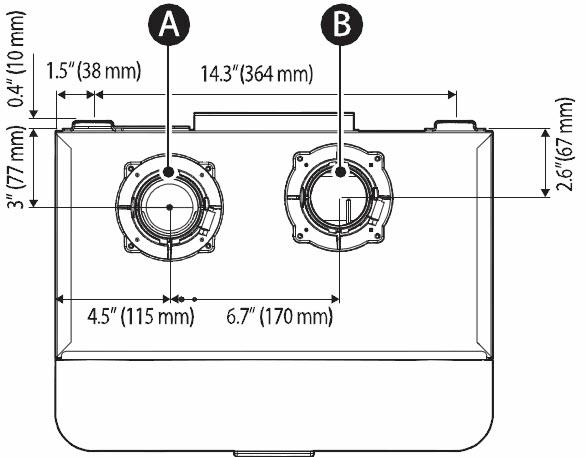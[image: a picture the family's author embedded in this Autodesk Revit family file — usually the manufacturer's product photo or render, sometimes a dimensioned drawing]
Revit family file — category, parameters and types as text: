
# Revit family: Water_Heater-Racks-Navien-NPE-2_Unit_Back_to_Back
name_source: partatom
category: Mechanical Equipment
revit_build: Autodesk Revit 2016 (Build: 20150220_1215(x64)
units: mm (PartAtom-declared; Revit-internal decimal feet)

## family parameters
Cut with Voids When Loaded = No
Host = Face
OmniClass Number = 23.65.35.11
OmniClass Title = Supply Water Heaters
Part Type = Normal
Room Calculation Point = No
Round Connector Dimension = Use Diameter
Shared = No

## types (4) — shared parameters
2" Exhaust/Intake = Yes
3" Exhaust/Intake = No
Apparent Load = 0 VA
Assembly Code = D3010500
Certifications = Energy Star | AHRI | CSA | CSA | NFS
Cold Water Inlet = 1"
Configuration = NPE_B2_2B
Default Elevation = 48 "
Depth = 23.8 "
Description = 2 Unit Back to Back
Exhaust = 2"
Finish = Metal - Navien - White
Flow Rate = 1 GPM
Flow Rate Note = 35°F (19°C) temp rise: 11.2 GPM (42 L/m) | 45°F (25°C) temp rise: 8.7 GPM (33 L/m) | 67°F (36°C) temp rise: NPE-240A: 5.6 GPM(21 L/m), NPE-240S: 5.7 GPM(22 L/m)
Frequency = 60 Hz
Gas Inlet = 1"
Heating Capacity = 120000.0 Btu/h
Heating Capacity Note = 19,900–199,900 (BTU/H)
Height = 65.5 "
Hot Water Outlet = 1"
Ignition = Electronic ignition
Installation Type = Indoor or Outdoor Wall-Hung
Intake = 2"
Keynote = 22 33 00.A1
Manifold(s) = (1) 30019043A + (1) 30019039A
Manufacturer = Navien, Inc.
Manufacturer Fax Number = (949) 420-0430
Natural Gas Manifold Pressure = -0.05" WC to -0.58" WC
Natural Gas Supply Pressure = 3.5"–10.5" WC
Number of Poles = 1
Phase = 1
Power Factor = 1
Product Documentation Link = https://www.navieninc.com
Product Name = NPE Series Tankless Water Heaters w/ Racks
Product Page URL = https://www.navieninc.com
Propane Gas Manifold Pressure = -0.10" WC to -0.78" WC
Propane Gas Supply Pressure = 8"–13" WC
Rack(s) = (1) GFFM-KDIZUS-003
Required Cascade Operation Accessory = (2) 30014367A (Common Vent Damper & Cascade Communication Cable) or (1) GXXX000546 (Individual Vent Cascade Communication Cable)
URL = https://www.navieninc.com
Venting = Exhaust: 2" PVC, CPVC, PP, SS / 2" special gas vent type BH (Class II, A/B/C) | Intake: 2" PVC, CPVC, PP, SS / 2" special gas vent type BH (Class II, A/B/C) | Vent clearances: 0" to combustibles
Venting Type = Forced draft direct vent
Version = 2016 - v1.0.a
Voltage = 120 V
Water Pressure = 15–150 PSI
Wi-Fi Ready = NaviLink Wi-Fi Control: PBCM-AS-001
Width = 23.3 "

## per-type parameters (varying)
| type | Constraints | Model | Natural Gas | Propane Gas | Recirculation Inlet | Recirculation Inlet Visibility | Tankless Water Heaters | Weight |
| Natural Gas - Recirculating System - NPE-240A(Advanced)-NG | 6 | (2) NPE-240A-NG | Yes | No | 0" | Yes | (2) NPE-240A-NG | 82.00 lbf |
| Natural Gas - NPE-240S(Standard)-NG | 7 | (2) NPE-240S-NG | Yes | No | 1" | No | (2) NPE-240S-NG | 75.00 lbf |
| Propane Gas - Recirculating System - NPE-240A(Advanced)-LPG | 6 | (2) NPE-240A-LPG | No | Yes | 0" | Yes | (2) NPE-240A-LPG | 82.00 lbf |
| Propane Gas - NPE-240S(Standard)-LPG | 7 | (2) NPE-240S-LPG | No | Yes | 1" | No | (2) NPE-240S-LPG | 75.00 lbf |

## geometry (parser evidence)
native form markers: Sweep x19
no freeform markers — native parametric forms only
